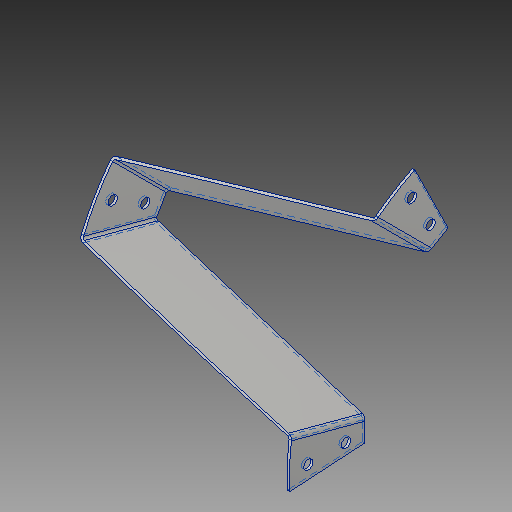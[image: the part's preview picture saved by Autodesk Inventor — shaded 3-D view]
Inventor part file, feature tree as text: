
AUTODESK INVENTOR PART (.ipt)
format: ipt  version: 2019 (Build 230136000, 136)  size: 273,920 bytes
history: native  units: in
note: dims shown in document units (in); Inventor stores cm internally (conversion verified against a paired STEP export)
features: sheet_metal_op x5, sketch x3, other x3, plane x2, extrude x1
ambient origin geometry x8: Origin, YZ Plane, XZ Plane, XY Plane, X Axis, Y Axis, Z Axis, Center Point
bodies: Solid1 (feature_tree)
feature tree (14):
  plane  "Work Plane1"
  plane  "Work Plane2"
  sketch  "Sketch1"  dims[d0=3.0in d1=-3.0in d2=12.0in]
  sketch  "Sketch2"  dims[d3=0.25in]
  sheet_metal_op  "Face1"
  sheet_metal_op  "Face2"
  sheet_metal_op  "Bend2"
  sheet_metal_op  "Bend3"
  extrude  "Extrusion1"  Depth=3.0in
  other  "Plate1"
  other  "Plate2"
  sheet_metal_op  "Bend1"
  sketch  "Sketch3"  dims[d4=1.0in d5=0.5in d6=4.7244in d8=360.0deg d10=0.5in d11=0.5in d12=0.0625in d13=0.0625in d14=0.0625in d15=0.0312in d16=0.125in d17=0.0625in d18=0.0625in d19=0.0312in d20=0.125in d21=0.0625in d22=0.0625in d23=0.0625in d24=0.0312in d25=0.125in d26=0.0625in d27=0.0625in d28=12.0in d29=20.0in d30=0.0in d31=0.0in d32=0.0625in]
  other  "Definition1"
